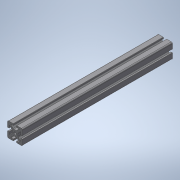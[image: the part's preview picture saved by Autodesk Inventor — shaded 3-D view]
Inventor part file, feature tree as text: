
AUTODESK INVENTOR PART (.ipt)
format: ipt  version: 2020.3 (Build 243373000, 373)  size: 252,928 bytes
history: native  units: in
note: dims shown in document units (in); Inventor stores cm internally (conversion verified against a paired STEP export)
features: extrude x1, sketch x1, projected_geometry x1
ambient origin geometry x8: Origin, YZ Plane, XZ Plane, XY Plane, X Axis, Y Axis, Z Axis, Center Point
bodies: Body1 (feature_tree)
feature tree (3):
  extrude  "Extrusion1"  [1 undecoded]
  sketch  "Sketch1"  dims[d0=15.775in d1=0.0in]
  projected_geometry  "Projected Loop1"
note: 1 required parameter value undecoded (feature->parameter linkage not recoverable at this tier; creation-order binding heuristic only, values carry confidence <= 0.55)
